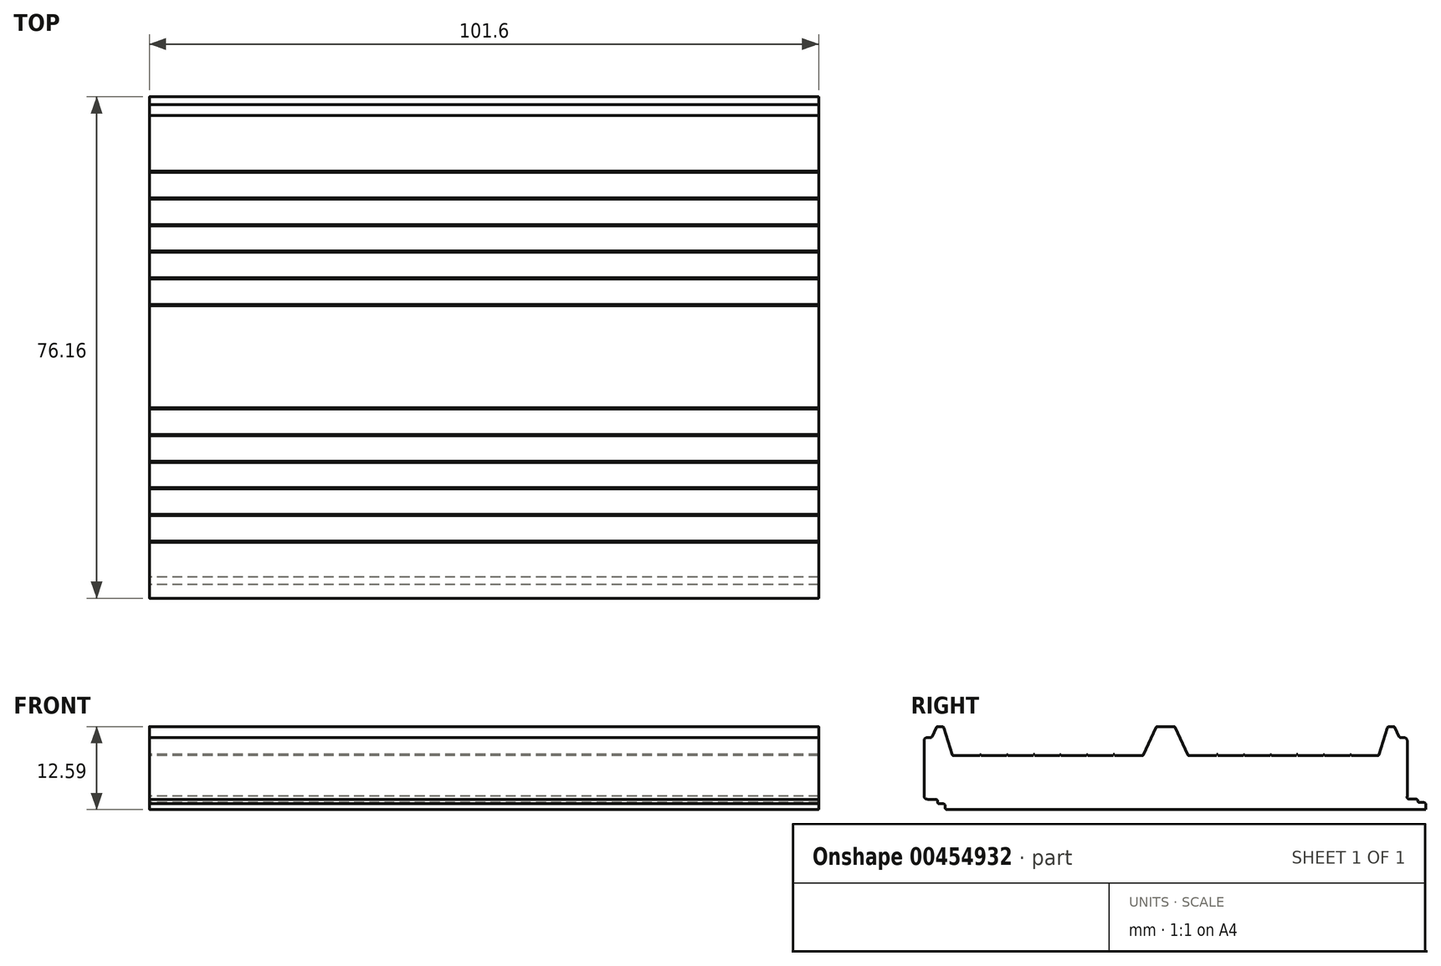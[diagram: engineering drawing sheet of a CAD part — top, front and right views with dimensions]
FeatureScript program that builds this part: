
annotation { "Feature Type Name" : "Feature", "Feature Type Description" : "" }
export const myFeature = defineFeature(function(context is Context, id is Id, definition is map)
    precondition{}
    {
        {
            var Q0;
            Q0=qCreatedBy(makeId("Right.planeOp"),FACE);
            var sketch = newSketch(context, id + "F0", { "sketchPlane" : qUnion([Q0])});
            skLineSegment(sketch, "E0", {"start": v(0, 0) * mm, "end": v(-33.21, 0) * mm});
            skLineSegment(sketch, "E1", {"start": v(-33.47, 0.25) * mm, "end": v(-33.47, 0.6) * mm});
            skLineSegment(sketch, "E2", {"start": v(-33.72, 0.85) * mm, "end": v(-34.37, 0.85) * mm});
            skLineSegment(sketch, "E3", {"start": v(-34.62, 1.1) * mm, "end": v(-34.62, 1.3) * mm});
            skLineSegment(sketch, "E4", {"start": v(-34.87, 1.55) * mm, "end": v(-36.16, 1.55) * mm});
            skLineSegment(sketch, "E5", {"start": v(-36.67, 2.05) * mm, "end": v(-36.67, 10.4) * mm});
            skLineSegment(sketch, "E6", {"start": v(-36.16, 10.92) * mm, "end": v(-35.67, 10.92) * mm});
            skLineSegment(sketch, "E7", {"start": v(-35.44, 11.06) * mm, "end": v(-34.8, 12.44) * mm});
            skLineSegment(sketch, "E8", {"start": v(-34.57, 12.59) * mm, "end": v(-33.9, 12.59) * mm});
            skLineSegment(sketch, "E9", {"start": v(-33.66, 12.4) * mm, "end": v(-32.4, 8.34) * mm});
            skLineSegment(sketch, "E10", {"start": v(-3.35, 8.3) * mm, "end": v(-1.46, 12.44) * mm});
            skLineSegment(sketch, "E11", {"start": v(-1.23, 12.59) * mm, "end": v(0, 12.59) * mm});
            skPoint(sketch, "E12.visualSharp", {"position": v(-36.67, 10.92) * mm});
            skArc(sketch, "E12.filletArc", {"start": v(-36.16, 10.92) * mm, "mid": v(-36.52, 10.77) * mm, "end": v(-36.67, 10.4) * mm});
            skPoint(sketch, "E13.visualSharp", {"position": v(-34.74, 12.59) * mm});
            skArc(sketch, "E13.filletArc", {"start": v(-34.57, 12.59) * mm, "mid": v(-34.71, 12.55) * mm, "end": v(-34.8, 12.44) * mm});
            skPoint(sketch, "E14.visualSharp", {"position": v(-33.72, 12.59) * mm});
            skArc(sketch, "E14.filletArc", {"start": v(-33.66, 12.4) * mm, "mid": v(-33.75, 12.54) * mm, "end": v(-33.9, 12.59) * mm});
            skPoint(sketch, "E15.visualSharp", {"position": v(-32.35, 8.16) * mm});
            skArc(sketch, "E15.filletArc", {"start": v(-32.4, 8.34) * mm, "mid": v(-32.32, 8.21) * mm, "end": v(-32.17, 8.16) * mm});
            skPoint(sketch, "E16.visualSharp", {"position": v(-35.5, 10.92) * mm});
            skArc(sketch, "E16.filletArc", {"start": v(-35.67, 10.92) * mm, "mid": v(-35.53, 10.96) * mm, "end": v(-35.44, 11.06) * mm});
            skPoint(sketch, "E17.visualSharp", {"position": v(-36.67, 1.55) * mm});
            skArc(sketch, "E17.filletArc", {"start": v(-36.67, 2.05) * mm, "mid": v(-36.52, 1.7) * mm, "end": v(-36.16, 1.55) * mm});
            skPoint(sketch, "E18.visualSharp", {"position": v(-34.62, 1.55) * mm});
            skArc(sketch, "E18.filletArc", {"start": v(-34.62, 1.3) * mm, "mid": v(-34.7, 1.47) * mm, "end": v(-34.87, 1.55) * mm});
            skPoint(sketch, "E19.visualSharp", {"position": v(-34.62, 0.85) * mm});
            skArc(sketch, "E19.filletArc", {"start": v(-34.62, 1.1) * mm, "mid": v(-34.55, 0.93) * mm, "end": v(-34.37, 0.85) * mm});
            skPoint(sketch, "E20.visualSharp", {"position": v(-33.47, 0.85) * mm});
            skArc(sketch, "E20.filletArc", {"start": v(-33.47, 0.6) * mm, "mid": v(-33.54, 0.78) * mm, "end": v(-33.72, 0.85) * mm});
            skPoint(sketch, "E21.visualSharp", {"position": v(-33.47, 0) * mm});
            skArc(sketch, "E21.filletArc", {"start": v(-33.47, 0.25) * mm, "mid": v(-33.4, 0.07) * mm, "end": v(-33.21, 0) * mm});
            skPoint(sketch, "E22.visualSharp", {"position": v(-1.39, 12.59) * mm});
            skArc(sketch, "E22.filletArc", {"start": v(-1.23, 12.59) * mm, "mid": v(-1.36, 12.55) * mm, "end": v(-1.46, 12.44) * mm});
            skPoint(sketch, "E23.visualSharp", {"position": v(-3.42, 8.16) * mm});
            skArc(sketch, "E23.filletArc", {"start": v(-3.58, 8.16) * mm, "mid": v(-3.44, 8.2) * mm, "end": v(-3.35, 8.3) * mm});
            skLineSegment(sketch, "E24", {"start": v(-32.17, 8.16) * mm, "end": v(-28.18, 8.16) * mm});
            skLineSegment(sketch, "E25", {"start": v(-28.18, 8.16) * mm, "end": v(-28.18, 8.34) * mm});
            skLineSegment(sketch, "E26", {"start": v(-28.18, 8.34) * mm, "end": v(-28, 8.34) * mm});
            skLineSegment(sketch, "E27", {"start": v(-28, 8.34) * mm, "end": v(-28, 8.16) * mm});
            skLineSegment(sketch, "E28", {"start": v(-28, 8.16) * mm, "end": v(-24.1, 8.16) * mm});
            skLineSegment(sketch, "E29", {"start": v(-24.1, 8.16) * mm, "end": v(-24.1, 8.34) * mm});
            skLineSegment(sketch, "E30", {"start": v(-24.1, 8.34) * mm, "end": v(-23.92, 8.34) * mm});
            skLineSegment(sketch, "E31", {"start": v(-23.92, 8.34) * mm, "end": v(-23.92, 8.16) * mm});
            skLineSegment(sketch, "E32", {"start": v(-23.92, 8.16) * mm, "end": v(-20.08, 8.16) * mm});
            skLineSegment(sketch, "E33", {"start": v(-20.08, 8.16) * mm, "end": v(-20.08, 8.35) * mm});
            skLineSegment(sketch, "E34", {"start": v(-20.08, 8.35) * mm, "end": v(-19.9, 8.35) * mm});
            skLineSegment(sketch, "E35", {"start": v(-19.9, 8.35) * mm, "end": v(-19.9, 8.16) * mm});
            skLineSegment(sketch, "E36", {"start": v(-19.9, 8.16) * mm, "end": v(-16.04, 8.16) * mm});
            skLineSegment(sketch, "E37", {"start": v(-16.04, 8.16) * mm, "end": v(-16.04, 8.34) * mm});
            skLineSegment(sketch, "E38", {"start": v(-16.04, 8.34) * mm, "end": v(-15.86, 8.34) * mm});
            skLineSegment(sketch, "E39", {"start": v(-15.86, 8.34) * mm, "end": v(-15.86, 8.16) * mm});
            skLineSegment(sketch, "E40", {"start": v(-15.86, 8.16) * mm, "end": v(-11.98, 8.16) * mm});
            skLineSegment(sketch, "E41", {"start": v(-11.98, 8.16) * mm, "end": v(-11.98, 8.33) * mm});
            skLineSegment(sketch, "E42", {"start": v(-11.98, 8.33) * mm, "end": v(-11.8, 8.33) * mm});
            skLineSegment(sketch, "E43", {"start": v(-11.8, 8.33) * mm, "end": v(-11.8, 8.16) * mm});
            skLineSegment(sketch, "E44", {"start": v(-11.8, 8.16) * mm, "end": v(-7.93, 8.16) * mm});
            skLineSegment(sketch, "E45", {"start": v(-7.93, 8.16) * mm, "end": v(-7.93, 8.35) * mm});
            skLineSegment(sketch, "E46", {"start": v(-7.93, 8.35) * mm, "end": v(-7.74, 8.35) * mm});
            skLineSegment(sketch, "E47", {"start": v(-7.74, 8.35) * mm, "end": v(-7.74, 8.16) * mm});
            skLineSegment(sketch, "E48", {"start": v(-7.74, 8.16) * mm, "end": v(-3.58, 8.16) * mm});
            skLineSegment(sketch, "E49.MirrorCS", {"start": v(36.16, 10.92) * mm, "end": v(35.67, 10.92) * mm});
            skArc(sketch, "E50.MirrorCS", {"start": v(34.57, 12.59) * mm, "mid": v(34.71, 12.55) * mm, "end": v(34.8, 12.44) * mm});
            skLineSegment(sketch, "E51.MirrorCS", {"start": v(35.44, 11.06) * mm, "end": v(34.8, 12.44) * mm});
            skArc(sketch, "E52.MirrorCS", {"start": v(36.16, 10.92) * mm, "mid": v(36.52, 10.77) * mm, "end": v(36.67, 10.4) * mm});
            skArc(sketch, "E53.MirrorCS", {"start": v(35.67, 10.92) * mm, "mid": v(35.53, 10.96) * mm, "end": v(35.44, 11.06) * mm});
            skLineSegment(sketch, "E54.MirrorCS", {"start": v(7.93, 8.35) * mm, "end": v(7.74, 8.35) * mm});
            skLineSegment(sketch, "E55.MirrorCS", {"start": v(16.04, 8.34) * mm, "end": v(15.86, 8.34) * mm});
            skLineSegment(sketch, "E56.MirrorCS", {"start": v(7.93, 8.16) * mm, "end": v(7.93, 8.35) * mm});
            skLineSegment(sketch, "E57.MirrorCS", {"start": v(24.1, 8.34) * mm, "end": v(23.92, 8.34) * mm});
            skLineSegment(sketch, "E58.MirrorCS", {"start": v(24.1, 8.16) * mm, "end": v(24.1, 8.34) * mm});
            skLineSegment(sketch, "E59.MirrorCS", {"start": v(16.04, 8.16) * mm, "end": v(16.04, 8.34) * mm});
            skArc(sketch, "E60.MirrorCS", {"start": v(32.4, 8.34) * mm, "mid": v(32.32, 8.21) * mm, "end": v(32.17, 8.16) * mm});
            skLineSegment(sketch, "E61.MirrorCS", {"start": v(20.08, 8.16) * mm, "end": v(20.08, 8.35) * mm});
            skLineSegment(sketch, "E62.MirrorCS", {"start": v(7.74, 8.35) * mm, "end": v(7.74, 8.16) * mm});
            skLineSegment(sketch, "E63.MirrorCS", {"start": v(23.92, 8.34) * mm, "end": v(23.92, 8.16) * mm});
            skArc(sketch, "E64.MirrorCS", {"start": v(33.66, 12.4) * mm, "mid": v(33.75, 12.54) * mm, "end": v(33.9, 12.59) * mm});
            skLineSegment(sketch, "E65.MirrorCS", {"start": v(34.57, 12.59) * mm, "end": v(33.9, 12.59) * mm});
            skArc(sketch, "E66.MirrorCS", {"start": v(3.58, 8.16) * mm, "mid": v(3.44, 8.2) * mm, "end": v(3.35, 8.3) * mm});
            skLineSegment(sketch, "E67.MirrorCS", {"start": v(15.86, 8.34) * mm, "end": v(15.86, 8.16) * mm});
            skArc(sketch, "E68.MirrorCS", {"start": v(1.23, 12.59) * mm, "mid": v(1.36, 12.55) * mm, "end": v(1.46, 12.44) * mm});
            skLineSegment(sketch, "E69.MirrorCS", {"start": v(19.9, 8.35) * mm, "end": v(19.9, 8.16) * mm});
            skLineSegment(sketch, "E70.MirrorCS", {"start": v(1.23, 12.59) * mm, "end": v(0, 12.59) * mm});
            skLineSegment(sketch, "E71.MirrorCS", {"start": v(20.08, 8.35) * mm, "end": v(19.9, 8.35) * mm});
            skLineSegment(sketch, "E72.MirrorCS", {"start": v(28.18, 8.16) * mm, "end": v(28.18, 8.34) * mm});
            skLineSegment(sketch, "E73.MirrorCS", {"start": v(28.18, 8.34) * mm, "end": v(28, 8.34) * mm});
            skLineSegment(sketch, "E74.MirrorCS", {"start": v(28, 8.34) * mm, "end": v(28, 8.16) * mm});
            skLineSegment(sketch, "E75.MirrorCS", {"start": v(11.98, 8.33) * mm, "end": v(11.8, 8.33) * mm});
            skLineSegment(sketch, "E76.MirrorCS", {"start": v(11.98, 8.16) * mm, "end": v(11.98, 8.33) * mm});
            skLineSegment(sketch, "E77.MirrorCS", {"start": v(11.8, 8.33) * mm, "end": v(11.8, 8.16) * mm});
            skPoint(sketch, "E78.MirrorP", {"position": v(3.42, 8.16) * mm});
            skPoint(sketch, "E79.MirrorP", {"position": v(32.35, 8.16) * mm});
            skLineSegment(sketch, "E80.MirrorCS", {"start": v(7.74, 8.16) * mm, "end": v(3.58, 8.16) * mm});
            skLineSegment(sketch, "E81.MirrorCS", {"start": v(32.17, 8.16) * mm, "end": v(28.18, 8.16) * mm});
            skPoint(sketch, "E82.MirrorP", {"position": v(36.67, 10.92) * mm});
            skLineSegment(sketch, "E83.MirrorCS", {"start": v(33.66, 12.4) * mm, "end": v(32.4, 8.34) * mm});
            skPoint(sketch, "E84.MirrorP", {"position": v(35.5, 10.92) * mm});
            skLineSegment(sketch, "E85.MirrorCS", {"start": v(15.86, 8.16) * mm, "end": v(11.98, 8.16) * mm});
            skLineSegment(sketch, "E86.MirrorCS", {"start": v(3.35, 8.3) * mm, "end": v(1.46, 12.44) * mm});
            skPoint(sketch, "E87.MirrorP", {"position": v(1.39, 12.59) * mm});
            skPoint(sketch, "E88.MirrorP", {"position": v(33.72, 12.59) * mm});
            skLineSegment(sketch, "E89.MirrorCS", {"start": v(36.67, 2.05) * mm, "end": v(36.67, 10.4) * mm});
            skLineSegment(sketch, "E90.MirrorCS", {"start": v(19.9, 8.16) * mm, "end": v(16.04, 8.16) * mm});
            skLineSegment(sketch, "E91.MirrorCS", {"start": v(28, 8.16) * mm, "end": v(24.1, 8.16) * mm});
            skPoint(sketch, "E92.MirrorP", {"position": v(34.74, 12.59) * mm});
            skLineSegment(sketch, "E93.MirrorCS", {"start": v(11.8, 8.16) * mm, "end": v(7.93, 8.16) * mm});
            skLineSegment(sketch, "E94.MirrorCS", {"start": v(23.92, 8.16) * mm, "end": v(20.08, 8.16) * mm});
            skLineSegment(sketch, "E95", {"start": v(36.92, 1.58) * mm, "end": v(38.03, 1.58) * mm});
            skLineSegment(sketch, "E96", {"start": v(38.28, 1.32) * mm, "end": v(38.28, 1.3) * mm});
            skLineSegment(sketch, "E97", {"start": v(38.53, 1.04) * mm, "end": v(39.24, 1.04) * mm});
            skLineSegment(sketch, "E98", {"start": v(39.5, 0.79) * mm, "end": v(39.5, 0) * mm});
            skLineSegment(sketch, "E99", {"start": v(36.67, 1.84) * mm, "end": v(36.67, 2.05) * mm});
            skPoint(sketch, "E100.visualSharp", {"position": v(38.28, 1.58) * mm});
            skArc(sketch, "E100.filletArc", {"start": v(38.28, 1.32) * mm, "mid": v(38.2, 1.5) * mm, "end": v(38.03, 1.58) * mm});
            skPoint(sketch, "E101.visualSharp", {"position": v(38.28, 1.04) * mm});
            skArc(sketch, "E101.filletArc", {"start": v(38.28, 1.3) * mm, "mid": v(38.36, 1.12) * mm, "end": v(38.53, 1.04) * mm});
            skPoint(sketch, "E102.visualSharp", {"position": v(39.5, 1.04) * mm});
            skArc(sketch, "E102.filletArc", {"start": v(39.5, 0.79) * mm, "mid": v(39.42, 0.97) * mm, "end": v(39.24, 1.04) * mm});
            skPoint(sketch, "E103.visualSharp", {"position": v(36.66, 1.58) * mm});
            skArc(sketch, "E103.filletArc", {"start": v(36.67, 1.84) * mm, "mid": v(36.74, 1.65) * mm, "end": v(36.92, 1.58) * mm});
            skLineSegment(sketch, "E104", {"start": v(39.5, 0) * mm, "end": v(0, 0) * mm});
            skSolve(sketch);
        }
        {
            var Q0;
            Q0 = qSketchRegion(id + "F0", true);
            extrude(context, id + "F1", {"entities" : qUnion([Q0]), "depth" : 50.8 * mm, "hasSecondDirection" : true, "secondDirectionOppositeDirection" : true, "secondDirectionDepth" : 50.8 * mm});
        }
    });
